# Revit family: Bathroom_Faucet-Commercial-Moen-90_Degree-One_Handle-S6700
name_source: partatom
category: Plumbing Fixtures
revit_build: Autodesk Revit 2015 (Build: 20140606_1530(x64)
units: mm (PartAtom-declared; Revit-internal decimal feet)

## types (1)
- S6700
    Assembly Code = D2010
    CW Connection = Yes
    CWFU = 0
    Cold Water Diameter = 0"
    Cold Water Radius = 0"
    Default Elevation = 4' - 0"
    Description = 90 Degree chrome one-handle bathroom faucet
    Domestic Water Flow Rate = 1.50 GPM
    Finish = Metal - Moen - Chrome
    Flow Rate = 1.50 GPM
    HW Connection = Yes
    HWFU = 0
    Height = 0' - 6 5/16"
    Hot Water Diameter = 0"
    Hot Water Radius = 0"
    Length = 0' - 4 1/4"
    Manufacturer = Moen Commercial
    Model = S6700
    Product Documentation Link = http://pro.moen.com
    Product Page URL = http://pro.moen.com
    Product data url = https://bimobject.com
    URL = http://pro.moen.com
    Vent Connection = Yes
    WFU = 0
    Waste Connection = Yes
    Width = 0' - 2 3/16"

## geometry (parser evidence)
native form markers: Blend x4, Sweep x2
no freeform markers — native parametric forms only
